# Revit family: SoapLiquidDispenser-Vitra-BaseSeries-A44107
name_source: partatom
category: Plumbing Fixtures
revit_build: Autodesk Revit 2017 (Build: 20160225_1515(x64)
units: mm (PartAtom-declared; Revit-internal decimal feet)

## family parameters
Cut with Voids When Loaded = No
Host = Face
OmniClass Number = 23.45.00.00
OmniClass Title = Sanitary, Laundry, and Cleaning Equipment
Part Type = Normal
Room Calculation Point = No
Round Connector Dimension = Use Diameter
Shared = Yes

## types (1)
- SoapLiquidDispenser-Vitra-BaseSeries-A44107
    Article No. (default) = A44107
    BIMobject category = Sanitary - Dispensers
    Brand = VitrA
    CW Connection = No
    Coating Material = Glass
    Default Elevation = 0 mm  [stored 0 ft]
    Description = Base Liquid Soap Dispenser
    Design country = Turkey
    HW Connection = No
    IFC Classification = Sanitary Terminal
    Main Material = Glass
    Manufacturer = Vitra
    Manufacturer name = Vitra
    Masterformat 2014 Code = 12 00 00
    Masterformat 2014 Description = Furnishings
    Model = A44107
    NBS Referans Code = 35-76-80
    NBS Referans Description = Soap Dispensers
    Nominal Depth (mm) = 120 mm
    Nominal Height (mm) = 170 mm
    Nominal Width (mm) = 71 mm
    OmniClass Code = 23-31 25 29 13
    OmniClass Description = Hand Soap Dispensers
    Primary Material = Chrome
    Product Properties = Liquid Soap Dispenser
    Product SKU = A44107
    Product Type = Liquid Soap Dispenser
    Product certification = https://www.vitraglobal.com
    Product family = BaseSeries
    Product group = Liquid Soap Dispenser
    Product url = https://vitraglobal.com
    Technical description = https://vitraglobal.com
    UNSPSC Description = Sanitary ware
    URL = https://vitraglobal.com
    Uniclass 1.4 Code = L8246
    Uniclass 1.4 Description = Soap holders/dispensers
    Uniclass 2.0 Code = PR-35-76-80
    Uniclass 2.0 Description = Soap Dispensers
    Uniclass 2015 Code = Pr_40_70_22_81
    Uniclass 2015 Name = Soap dispensers
    Uniformat II Code = E20
    Uniformat II Description = FURNISHINGS
    Vent Connection = No
    Warranty Period (Year) = 5 years
    Waste Connection = No
    Weight Net (kg) = 1
    Youtube = https://www.youtube.com

note: [stored X ft] marks values corroborated as IEEE doubles in the binary element streams (Revit-internal decimal feet)

## geometry (parser evidence)
native form markers: Sweep x1
no freeform markers — native parametric forms only
